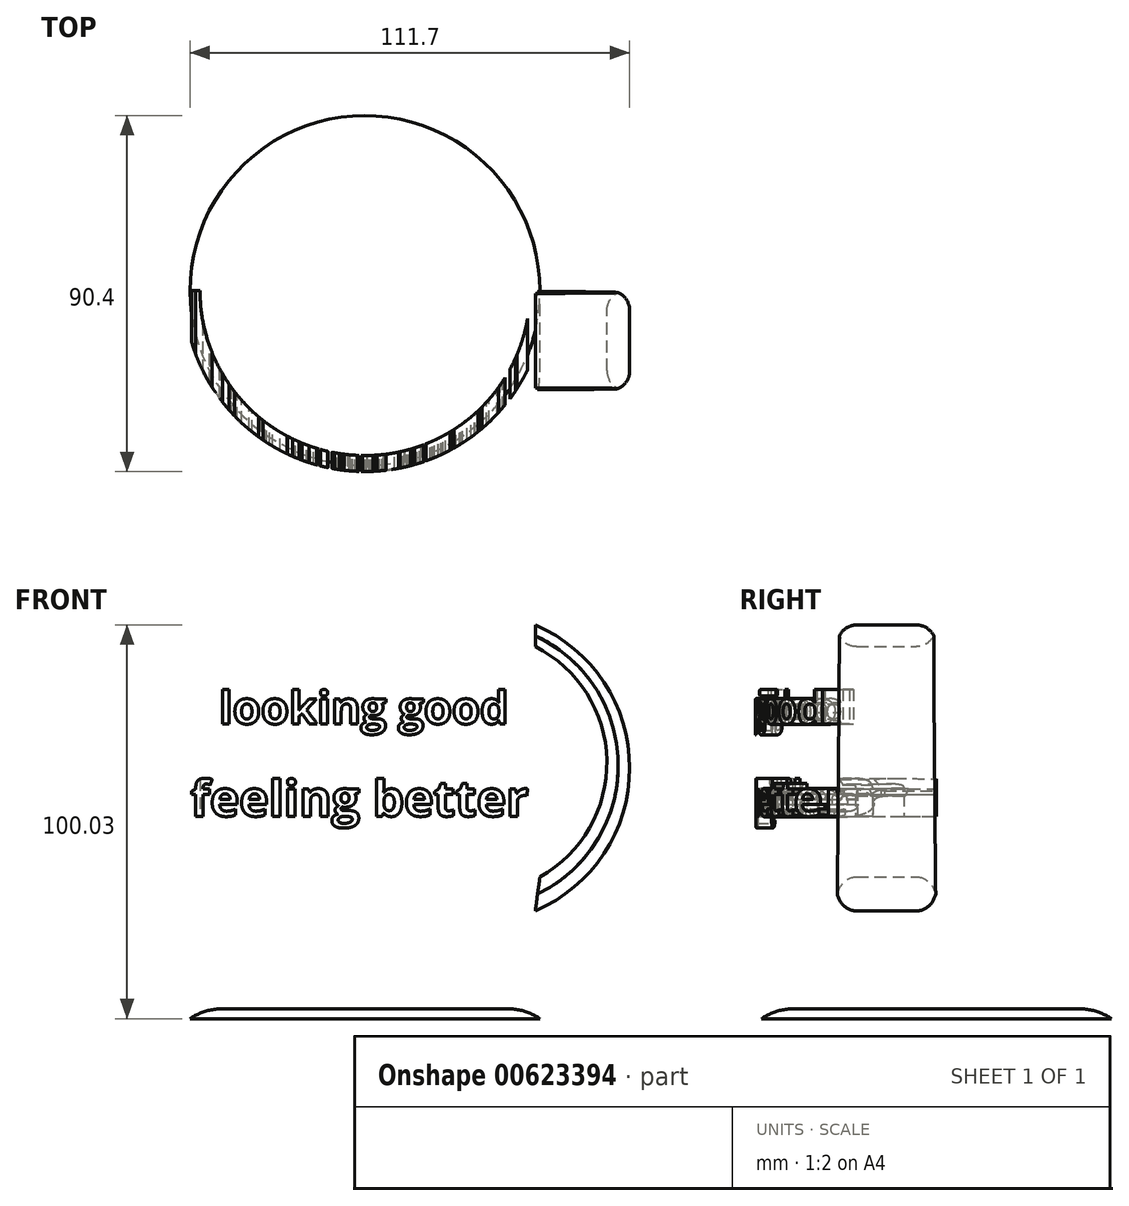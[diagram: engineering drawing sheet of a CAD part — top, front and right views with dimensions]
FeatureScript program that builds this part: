
annotation { "Feature Type Name" : "Feature", "Feature Type Description" : "" }
export const myFeature = defineFeature(function(context is Context, id is Id, definition is map)
    precondition{}
    {
        {
            var Q0;
            Q0=qCreatedBy(makeId("Top.planeOp"),FACE);
            var sketch = newSketch(context, id + "F0", { "sketchPlane" : qUnion([Q0])});
            skCircle(sketch, "E0", {"center": v(0, 0) * mm, "radius": 44.45 * mm});
            skCircle(sketch, "E1", {"center": v(0, 0) * mm, "radius": 42.26 * mm});
            skSolve(sketch);
        }
        {
            var Q0;
            Q0=sQuery(id+"F0.wireOp",EDGE,"E0");
            var Q1;
            Q1=sQuery(id+"F0.wireOp",EDGE,"E1");
            extrude(context, id + "F1", {"bodyType" : ToolBodyType.SURFACE, "surfaceEntities" : qUnion([Q0, Q1]), "depth" : 121 * mm, "offsetDistance" : 25.4 * mm});
        }
        {
            var Q0;
            Q0=qCreatedBy(makeId("Front.planeOp"),FACE);
            var sketch = newSketch(context, id + "F2", { "sketchPlane" : qUnion([Q0])});
            skText(sketch, "E2", { "text": "looking good", "fontName": "OpenSans-Bold.ttf"});
            skText(sketch, "E3", { "text": "feeling better", "fontName": "OpenSans-Bold.ttf"});
            const initialGuessF2  = {"E2": [-0.0371, 0.0749, 1, 0, 0.0083], "E3": [-0.04426, 0.05144, 1, 0, 0.00909]};
            skSetInitialGuess(sketch, initialGuessF2);
            skSolve(sketch);
        }
        {
            var Q0;
            Q0 = qSketchRegion(id + "F2", true);
            extrude(context, id + "F3", {"entities" : qUnion([Q0]), "depth" : 50.8 * mm, "offsetDistance" : 25.4 * mm});
        }
        {
            var Q0;
            Q0=qCreatedBy(makeId("Front.planeOp"),FACE);
            var sketch = newSketch(context, id + "F4", { "sketchPlane" : qUnion([Q0])});
            skLineSegment(sketch, "E4", {"start": v(0, 0) * mm, "end": v(0, 187.67) * mm});
            skLineSegment(sketch, "E5.0", {"start": v(44.45, 121) * mm, "end": v(-44.45, 121) * mm});
            skLineSegment(sketch, "E6", {"start": v(-44.45, 0) * mm, "end": v(-44.45, 121) * mm});
            skLineSegment(sketch, "E7", {"start": v(44.45, 121) * mm, "end": v(44.45, 0) * mm});
            skLineSegment(sketch, "E8.0", {"start": v(-44.45, 0) * mm, "end": v(44.45, 0) * mm});
            skLineSegment(sketch, "E9.0", {"start": v(-45.95, -1.5) * mm, "end": v(-38.4, -1.5) * mm});
            skLineSegment(sketch, "E9.1", {"start": v(-45.95, -1.5) * mm, "end": v(-45.95, 122.5) * mm});
            skLineSegment(sketch, "E10", {"start": v(-31.43, 122.5) * mm, "end": v(-26.64, 157.77) * mm});
            skLineSegment(sketch, "E11", {"start": v(-26.64, 157.77) * mm, "end": v(-57.97, 166.47) * mm});
            skLineSegment(sketch, "E12", {"start": v(-57.97, 166.47) * mm, "end": v(-95.39, 121.66) * mm});
            skLineSegment(sketch, "E13", {"start": v(-95.39, 121.66) * mm, "end": v(-111.92, 52.48) * mm});
            skLineSegment(sketch, "E14", {"start": v(-111.92, 52.48) * mm, "end": v(-93.21, -4.09) * mm});
            skLineSegment(sketch, "E15", {"start": v(-93.21, -4.09) * mm, "end": v(-66.67, -30.2) * mm});
            skLineSegment(sketch, "E16", {"start": v(-66.67, -30.2) * mm, "end": v(-33.6, -30.2) * mm});
            skLineSegment(sketch, "E17", {"start": v(-33.6, -30.2) * mm, "end": v(-38.4, -1.5) * mm});
            skLineSegment(sketch, "E18.trimOffspring", {"start": v(-31.43, 122.5) * mm, "end": v(-45.95, 122.5) * mm});
            skSolve(sketch);
        }
        {
            var Q0;
            Q0=makeQuery(id+"F4.imprint","IMPRINT",FACE,{"disambiguationData":[TD([[makeQuery(id+"F4.imprint","IMPRINT",EDGE,{"derivedFrom":sQuery(id+"F4.wireOp",EDGE,"E9.0")}),-1.0]])]});
            var Q1;
            Q1=sQuery(id+"F4.wireOp",EDGE,"E4");
            revolve(context, id + "F5", {"operationType" : NewBodyOperationType.REMOVE, "entities" : qUnion([Q0]), "axis" : qUnion([Q1]), "revolveType" : RevolveType.FULL});
        }
        {
            var Q0;
            Q0=qCreatedBy(makeId("Top.planeOp"),FACE);
            var sketch = newSketch(context, id + "F6", { "sketchPlane" : qUnion([Q0])});
            skCircle(sketch, "E19", {"center": v(0, 0) * mm, "radius": 41.91 * mm});
            skSolve(sketch);
        }
        {
            var Q0;
            Q0 = qSketchRegion(id + "F6", true);
            extrude(context, id + "F7", {"entities" : qUnion([Q0]), "operationType" : NewBodyOperationType.REMOVE, "depth" : 94.23 * mm, "offsetDistance" : 25.4 * mm});
        }
        {
            var Q0;
            Q0=qCreatedBy(makeId("Top.planeOp"),FACE);
            var sketch = newSketch(context, id + "F8", { "sketchPlane" : qUnion([Q0])});
            skCircle(sketch, "E20", {"center": v(0, 0) * mm, "radius": 44.45 * mm});
            skSolve(sketch);
        }
        {
            var Q0;
            Q0 = qSketchRegion(id + "F8", true);
            extrude(context, id + "F9", {"entities" : qUnion([Q0]), "depth" : 2.54 * mm, "offsetDistance" : 25.4 * mm});
        }
        {
            var Q0;
            Q0=makeQuery(id+"F9.opExtrude","CAP_FACE",FACE,{"disambiguationData":[OSD([sQuery(id+"F8.wireOp",EDGE,"E20")])],"isStart":false});
            fillet(context, id + "F10", {"entities" : qUnion([Q0]), "radius" : 15.33 * mm, "tangentPropagation" : true, "allowEdgeOverflow" : false});
        }
        {
            var Q0;
            Q0=qCreatedBy(makeId("Front.planeOp"),FACE);
            var sketch = newSketch(context, id + "F11", { "sketchPlane" : qUnion([Q0])});
            skArc(sketch, "E21", {"start": v(44.45, 36.03) * mm, "mid": v(61.46, 65.63) * mm, "end": v(43.27, 94.52) * mm});
            skArc(sketch, "E22", {"start": v(43.27, 27.35) * mm, "mid": v(67.25, 63.7) * mm, "end": v(43.27, 100.03) * mm});
            skLineSegment(sketch, "E23", {"start": v(43.27, 94.52) * mm, "end": v(43.27, 100.03) * mm});
            skLineSegment(sketch, "E24", {"start": v(43.27, 27.35) * mm, "end": v(44.45, 36.03) * mm});
            skSolve(sketch);
        }
        {
            var Q0;
            Q0 = qSketchRegion(id + "F11", true);
            extrude(context, id + "F12", {"entities" : qUnion([Q0]), "depth" : 25.4 * mm, "offsetDistance" : 25.4 * mm});
        }
        {
            var Q0;
            Q0=makeQuery(id+"F12.opExtrude","CAP_EDGE",EDGE,{"disambiguationData":[OSD([sQuery(id+"F11.wireOp",EDGE,"E21")])],"isStart":false});
            var Q1;
            Q1=makeQuery(id+"F12.opExtrude","CAP_EDGE",EDGE,{"disambiguationData":[OSD([sQuery(id+"F11.wireOp",EDGE,"E22")])],"isStart":false});
            var Q2;
            Q2=makeQuery(id+"F12.opExtrude","CAP_EDGE",EDGE,{"disambiguationData":[OSD([sQuery(id+"F11.wireOp",EDGE,"E22")])],"isStart":true});
            var Q3;
            Q3=makeQuery(id+"F12.opExtrude","CAP_EDGE",EDGE,{"disambiguationData":[OSD([sQuery(id+"F11.wireOp",EDGE,"E21")])],"isStart":true});
            var Q4;
            Q4=makeQuery(id+"F1.opExtrude","SWEPT_FACE",FACE,{"disambiguationData":[OSD([sQuery(id+"F0.wireOp",EDGE,"E1")])]});
            fillet(context, id + "F13", {"entities" : qUnion([Q0, Q1, Q2, Q3, Q4]), "radius" : 5.08 * mm, "tangentPropagation" : true, "allowEdgeOverflow" : false});
        }
    });
